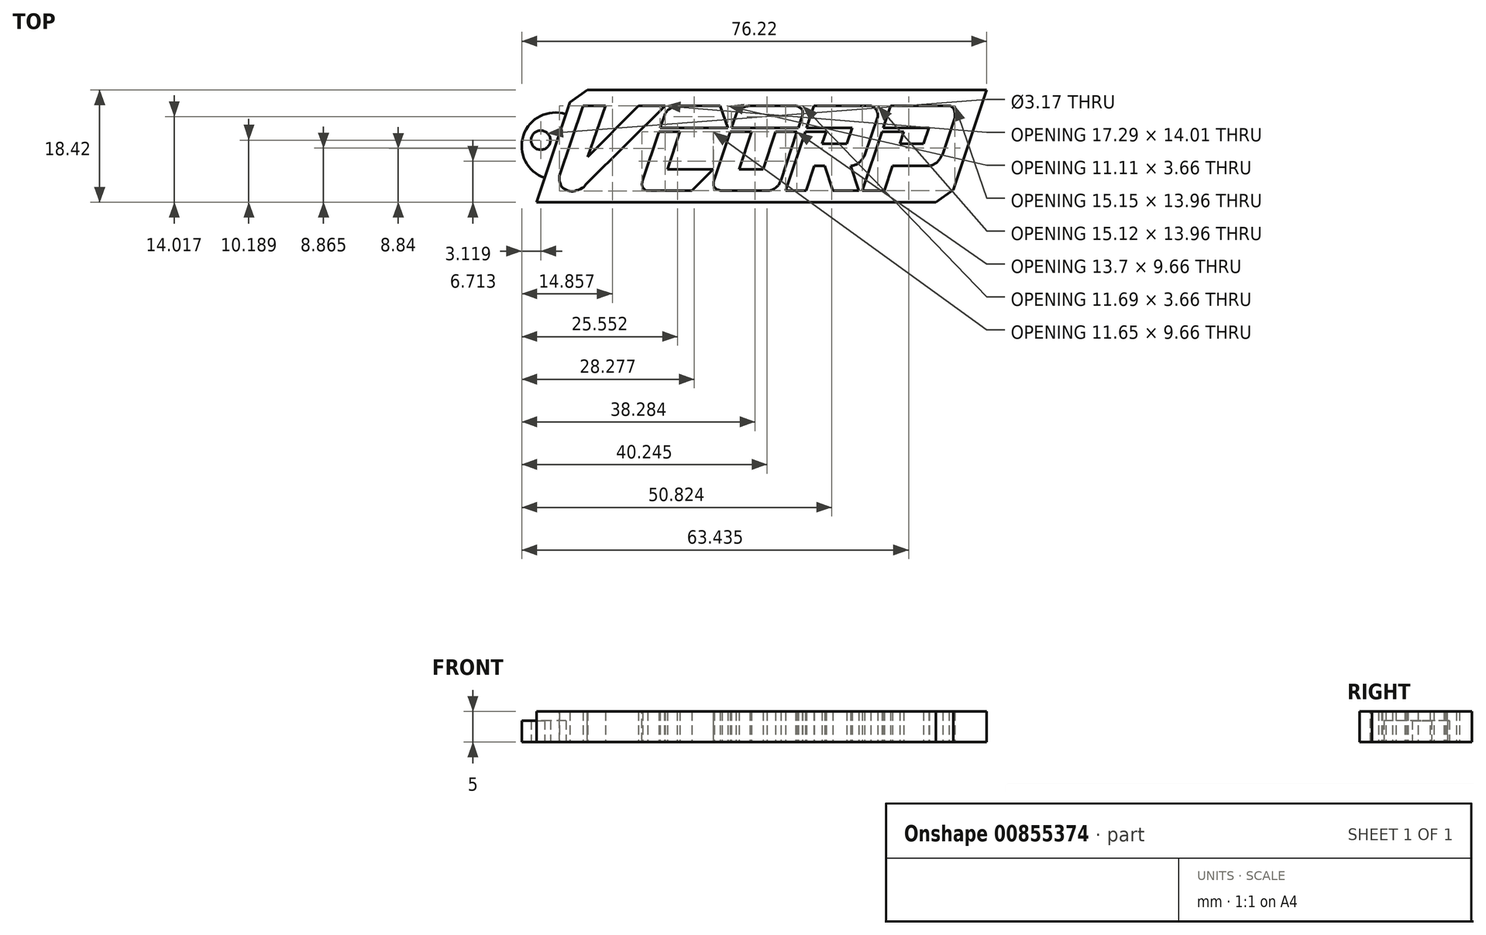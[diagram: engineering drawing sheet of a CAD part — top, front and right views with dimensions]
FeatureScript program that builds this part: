
annotation { "Feature Type Name" : "Feature", "Feature Type Description" : "" }
export const myFeature = defineFeature(function(context is Context, id is Id, definition is map)
    precondition{}
    {
        {
            var Q0;
            Q0=qCreatedBy(makeId("Top.planeOp"),FACE);
            var sketch = newSketch(context, id + "F0", { "sketchPlane" : qUnion([Q0])});
            skLineSegment(sketch, "E0", {"start": v(-25.15, 16.9) * mm, "end": v(-21.45, 16.9) * mm});
            skLineSegment(sketch, "E1", {"start": v(-25.15, 16.9) * mm, "end": v(-28.98, 5.4) * mm});
            skLineSegment(sketch, "E2", {"start": v(-21.45, 16.9) * mm, "end": v(-24.34, 8.47) * mm});
            skLineSegment(sketch, "E3", {"start": v(-24.34, 8.47) * mm, "end": v(-16.03, 16.9) * mm});
            skLineSegment(sketch, "E4", {"start": v(-11.69, 16.9) * mm, "end": v(-24.5, 4.15) * mm});
            skLineSegment(sketch, "E5", {"start": v(-12.47, 13.25) * mm, "end": v(-1.36, 13.25) * mm});
            skLineSegment(sketch, "E6", {"start": v(-12.69, 12.6) * mm, "end": v(-9.23, 12.6) * mm});
            skLineSegment(sketch, "E7", {"start": v(-12.69, 12.6) * mm, "end": v(-15.33, 4.67) * mm});
            skLineSegment(sketch, "E8", {"start": v(-12.47, 13.25) * mm, "end": v(-11.8, 15.25) * mm});
            skLineSegment(sketch, "E9", {"start": v(14.07, 10.63) * mm, "end": v(18.1, 10.63) * mm});
            skLineSegment(sketch, "E10", {"start": v(-11.27, 6.48) * mm, "end": v(-3.81, 6.48) * mm});
            skLineSegment(sketch, "E11", {"start": v(-9.23, 12.6) * mm, "end": v(-11.27, 6.48) * mm});
            skLineSegment(sketch, "E12", {"start": v(-3.81, 6.48) * mm, "end": v(-7.26, 2.94) * mm});
            skLineSegment(sketch, "E13", {"start": v(-7.26, 2.94) * mm, "end": v(-14.55, 2.94) * mm});
            skLineSegment(sketch, "E14", {"start": v(-1, 12.6) * mm, "end": v(-3.6, 4.78) * mm});
            skLineSegment(sketch, "E15", {"start": v(9.94, 12.6) * mm, "end": v(7.3, 4.65) * mm});
            skLineSegment(sketch, "E16", {"start": v(12.8, 7) * mm, "end": v(14.5, 7) * mm});
            skLineSegment(sketch, "E17", {"start": v(-2.35, 2.94) * mm, "end": v(5.02, 2.94) * mm});
            skLineSegment(sketch, "E18", {"start": v(12.72, 16.9) * mm, "end": v(11.5, 13.25) * mm});
            skLineSegment(sketch, "E19", {"start": v(12.8, 7) * mm, "end": v(11.46, 2.94) * mm});
            skLineSegment(sketch, "E20", {"start": v(14.5, 7) * mm, "end": v(15.82, 2.94) * mm});
            skLineSegment(sketch, "E21", {"start": v(18.74, 7.02) * mm, "end": v(20.05, 2.94) * mm});
            skLineSegment(sketch, "E22", {"start": v(25.32, 16.9) * mm, "end": v(24.1, 13.25) * mm});
            skLineSegment(sketch, "E23", {"start": v(27.48, 12.6) * mm, "end": v(26.82, 10.63) * mm});
            skLineSegment(sketch, "E24", {"start": v(35.81, 14.93) * mm, "end": v(33.83, 8.98) * mm});
            skLineSegment(sketch, "E25", {"start": v(25.62, 7.02) * mm, "end": v(31.6, 7.02) * mm});
            skLineSegment(sketch, "E26", {"start": v(23.18, 15.1) * mm, "end": v(21.06, 8.72) * mm});
            skLineSegment(sketch, "E27", {"start": v(31.58, 13.25) * mm, "end": v(30.7, 10.63) * mm});
            skLineSegment(sketch, "E28", {"start": v(18.98, 13.25) * mm, "end": v(18.1, 10.63) * mm});
            skLineSegment(sketch, "E29", {"start": v(14.07, 10.63) * mm, "end": v(14.73, 12.6) * mm});
            skLineSegment(sketch, "E30", {"start": v(10.16, 13.25) * mm, "end": v(10.81, 15.2) * mm});
            skLineSegment(sketch, "E31", {"start": v(-0.8, 13.25) * mm, "end": v(-0.07, 15.42) * mm});
            skLineSegment(sketch, "E32", {"start": v(-2.64, 16.9) * mm, "end": v(-1.36, 13.25) * mm});
            skFitSpline(sketch, "E33", {"points": [v(-11.8, 15.25) * mm, v(-11.34, 16.05) * mm, v(-10.56, 16.57) * mm, v(-9.7, 16.9) * mm], "startDerivative": vector(1.16, 2.59) * mm, "endDerivative": vector(2.61, 0.9) * mm});
            skFitSpline(sketch, "E34", {"points": [v(-15.33, 4.67) * mm, v(-15.47, 4.02) * mm, v(-15.33, 3.52) * mm, v(-14.9, 3.05) * mm, v(-14.55, 2.94) * mm], "startDerivative": vector(-0.94, -2.18) * mm, "endDerivative": vector(1.72, -0.28) * mm});
            skFitSpline(sketch, "E35", {"points": [v(-28.98, 5.4) * mm, v(-28.98, 4.67) * mm, v(-28.65, 3.64) * mm, v(-27.99, 3.12) * mm, v(-27.1, 2.86) * mm, v(-26.12, 3.05) * mm, v(-25.03, 3.56) * mm, v(-24.5, 4.15) * mm], "startDerivative": vector(-0.34, -5.3) * mm, "endDerivative": vector(3.8, 3.3) * mm});
            skFitSpline(sketch, "E36", {"points": [v(-3.6, 4.78) * mm, v(-3.76, 4.15) * mm, v(-3.6, 3.56) * mm, v(-3.24, 3.2) * mm, v(-2.87, 3.07) * mm, v(-2.35, 2.94) * mm], "startDerivative": vector(-0.85, -3) * mm, "endDerivative": vector(2.5, -0.4) * mm});
            skFitSpline(sketch, "E37", {"points": [v(5.02, 2.94) * mm, v(5.92, 3.12) * mm, v(6.74, 3.7) * mm, v(7.12, 4.23) * mm, v(7.3, 4.65) * mm], "startDerivative": vector(3.25, 0.3) * mm, "endDerivative": vector(0.81, 2.09) * mm});
            skFitSpline(sketch, "E38", {"points": [v(-0.07, 15.42) * mm, v(0.26, 15.96) * mm, v(0.8, 16.43) * mm, v(1.51, 16.76) * mm, v(2.24, 16.9) * mm], "startDerivative": vector(1.2, 2.4) * mm, "endDerivative": vector(2.87, 0.42) * mm});
            skFitSpline(sketch, "E39", {"points": [v(9.75, 16.9) * mm, v(10.38, 16.62) * mm, v(10.85, 16.08) * mm, v(10.89, 15.52) * mm, v(10.81, 15.2) * mm], "startDerivative": vector(2.34, -0.83) * mm, "endDerivative": vector(-0.45, -1.52) * mm});
            skFitSpline(sketch, "E40", {"points": [v(22.06, 16.9) * mm, v(22.75, 16.46) * mm, v(23.16, 15.72) * mm, v(23.18, 15.1) * mm], "startDerivative": vector(2.14, -1.05) * mm, "endDerivative": vector(-0.12, -2) * mm});
            skFitSpline(sketch, "E41", {"points": [v(18.74, 7.02) * mm, v(19.72, 7.3) * mm, v(20.54, 8) * mm, v(21.06, 8.72) * mm], "startDerivative": vector(3, 0.51) * mm, "endDerivative": vector(1.52, 2.24) * mm});
            skFitSpline(sketch, "E42", {"points": [v(34.9, 16.9) * mm, v(35.38, 16.7) * mm, v(35.74, 16.13) * mm, v(35.81, 15.5) * mm, v(35.81, 14.93) * mm], "startDerivative": vector(2.22, -0.58) * mm, "endDerivative": vector(-0.1, -1.37) * mm});
            skFitSpline(sketch, "E43", {"points": [v(31.6, 7.02) * mm, v(32.56, 7.37) * mm, v(33.28, 8.06) * mm, v(33.83, 8.98) * mm], "startDerivative": vector(3.03, 0.82) * mm, "endDerivative": vector(1.54, 2.8) * mm});
            skLineSegment(sketch, "E44", {"start": v(2.47, 12.6) * mm, "end": v(0.43, 6.48) * mm});
            skLineSegment(sketch, "E45", {"start": v(6.4, 12.6) * mm, "end": v(4.37, 6.48) * mm});
            skLineSegment(sketch, "E46.trimOffspring", {"start": v(-16.03, 16.9) * mm, "end": v(-11.69, 16.9) * mm});
            skLineSegment(sketch, "E47.trimOffspring", {"start": v(-9.7, 16.9) * mm, "end": v(-2.64, 16.9) * mm});
            skLineSegment(sketch, "E48.trimOffspring", {"start": v(2.24, 16.9) * mm, "end": v(9.75, 16.9) * mm});
            skLineSegment(sketch, "E49.trimOffspring", {"start": v(12.72, 16.9) * mm, "end": v(22.06, 16.9) * mm});
            skLineSegment(sketch, "E50.trimOffspring", {"start": v(25.32, 16.9) * mm, "end": v(34.9, 16.9) * mm});
            skLineSegment(sketch, "E51.trimOffspring", {"start": v(26.82, 10.63) * mm, "end": v(30.7, 10.63) * mm});
            skLineSegment(sketch, "E52.trimOffspring", {"start": v(25.62, 7.02) * mm, "end": v(24.26, 2.94) * mm});
            skLineSegment(sketch, "E53.trimOffspring", {"start": v(23.89, 12.6) * mm, "end": v(20.67, 2.94) * mm});
            skLineSegment(sketch, "E54.trimOffspring", {"start": v(24.1, 13.25) * mm, "end": v(31.58, 13.25) * mm});
            skLineSegment(sketch, "E55.trimOffspring", {"start": v(23.89, 12.6) * mm, "end": v(27.48, 12.6) * mm});
            skLineSegment(sketch, "E56.trimOffspring", {"start": v(20.67, 2.94) * mm, "end": v(24.26, 2.94) * mm});
            skLineSegment(sketch, "E57.trimOffspring", {"start": v(15.82, 2.94) * mm, "end": v(20.05, 2.94) * mm});
            skLineSegment(sketch, "E58.trimOffspring", {"start": v(8.07, 2.94) * mm, "end": v(11.46, 2.94) * mm});
            skLineSegment(sketch, "E59.trimOffspring", {"start": v(11.29, 12.6) * mm, "end": v(14.73, 12.6) * mm});
            skLineSegment(sketch, "E60.trimOffspring", {"start": v(11.29, 12.6) * mm, "end": v(8.07, 2.94) * mm});
            skLineSegment(sketch, "E61.trimOffspring", {"start": v(11.5, 13.25) * mm, "end": v(18.98, 13.25) * mm});
            skLineSegment(sketch, "E62.trimOffspring", {"start": v(6.4, 12.6) * mm, "end": v(9.94, 12.6) * mm});
            skLineSegment(sketch, "E63.trimOffspring", {"start": v(-0.8, 13.25) * mm, "end": v(10.16, 13.25) * mm});
            skLineSegment(sketch, "E64.trimOffspring", {"start": v(-1, 12.6) * mm, "end": v(2.47, 12.6) * mm});
            skLineSegment(sketch, "E65.trimOffspring", {"start": v(0.43, 6.48) * mm, "end": v(4.37, 6.48) * mm});
            skLineSegment(sketch, "E66", {"start": v(-26.62, 19.48) * mm, "end": v(-32.76, 1.06) * mm});
            skLineSegment(sketch, "E67", {"start": v(-32.76, 1.06) * mm, "end": v(34.9, 1.06) * mm});
            skLineSegment(sketch, "E68", {"start": v(34.9, 1.06) * mm, "end": v(41.03, 19.48) * mm});
            skLineSegment(sketch, "E69", {"start": v(41.03, 19.48) * mm, "end": v(-26.62, 19.48) * mm});
            skArc(sketch, "E70", {"start": v(-27.95, 15.5) * mm, "mid": v(-34.9, 12.01) * mm, "end": v(-31.43, 5.05) * mm});
            skCircle(sketch, "E71", {"center": v(-32.07, 11.25) * mm, "radius": 1.59 * mm});
            skSolve(sketch);
        }
        {
            var Q0;
            {var subQ0=sQuery(id+"F0.wireOp",EDGE,"E70");Q0=makeQuery(id+"F0.imprint","IMPRINT",FACE,{"disambiguationData":[TD([[makeQuery(id+"F0.imprint","IMPRINT",EDGE,{"derivedFrom":subQ0}),1.0]])]});}
            extrude(context, id + "F1", {"entities" : qUnion([Q0]), "depth" : 3.5 * mm, "offsetDistance" : 25 * mm});
        }
        {
            var Q0;
            Q0=makeQuery(id+"F0.imprint","IMPRINT",FACE,{"disambiguationData":[TD([[makeQuery(id+"F0.imprint","IMPRINT",EDGE,{"derivedFrom":sQuery(id+"F0.wireOp",EDGE,"E0")}),1.0]])]});
            extrude(context, id + "F2", {"entities" : qUnion([Q0]), "operationType" : NewBodyOperationType.ADD, "depth" : 5 * mm, "offsetDistance" : 25 * mm});
        }
        {
            var Q0;
            Q0=makeQuery(id+"F2.opExtrude","SWEPT_EDGE",EDGE,{"disambiguationData":[OSD([sQuery(id+"F0.wireOp",EDGE,"E66"),sQuery(id+"F0.wireOp",EDGE,"E69")])]});
            var Q1;
            Q1=makeQuery(id+"F2.opExtrude","SWEPT_EDGE",EDGE,{"disambiguationData":[OSD([sQuery(id+"F0.wireOp",EDGE,"E67"),sQuery(id+"F0.wireOp",EDGE,"E68")])]});
            chamfer(context, id + "F3", {"entities" : qUnion([Q0, Q1]), "width" : 3 * mm, "tangentPropagation" : true});
        }
    });
